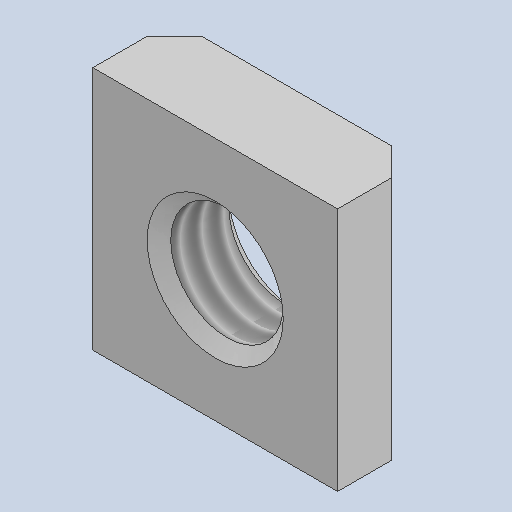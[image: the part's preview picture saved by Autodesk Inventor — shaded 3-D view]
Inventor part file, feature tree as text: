
AUTODESK INVENTOR PART (.ipt)
format: ipt  version: 2022 (Build 260153000, 153)  size: 134,144 bytes
history: native  units: in
note: dims shown in document units (in); Inventor stores cm internally (conversion verified against a paired STEP export)
features: other x3, sketch x3, plane x1
ambient origin geometry x8: Origin, YZ Plane, XZ Plane, XY Plane, X Axis, Y Axis, Z Axis, Center Point
bodies: Solid1 (feature_tree)
feature tree (7):
  other  "T-Nut Block M5  Threads.ipt"
  other  "Solid1::T-Nut Block M5  Threads.ipt"
  other  "TaggingFeature1"
  sketch  "Sketch_1"  dims[d0=0.3937in]
  sketch  "Sketch_2"
  sketch  "Sketch_3"
  plane  "Work Plane1"
